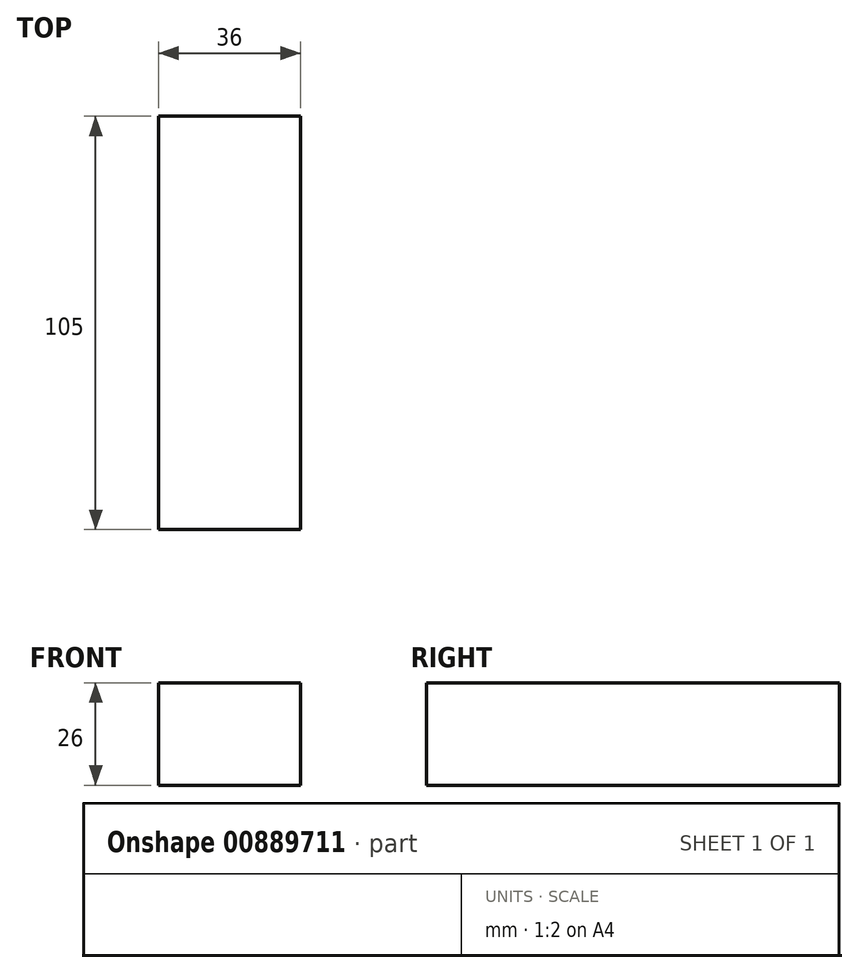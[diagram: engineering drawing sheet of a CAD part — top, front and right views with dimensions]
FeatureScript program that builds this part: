
annotation { "Feature Type Name" : "Feature", "Feature Type Description" : "" }
export const myFeature = defineFeature(function(context is Context, id is Id, definition is map)
    precondition{}
    {
        {
            var Q0;
            Q0=qCreatedBy(makeId("Top.planeOp"), FACE);
            var sketch = newSketch(context, id + "F0", { "sketchPlane" : qUnion([Q0])});
            skLineSegment(sketch, "E0.bottom", {"start": v(18, -52.5) * mm, "end": v(-18, -52.5) * mm});
            skLineSegment(sketch, "E0.top", {"start": v(18, 52.5) * mm, "end": v(-18, 52.5) * mm});
            skLineSegment(sketch, "E0.left", {"start": v(18, -52.5) * mm, "end": v(18, 52.5) * mm});
            skLineSegment(sketch, "E0.right", {"start": v(-18, -52.5) * mm, "end": v(-18, 52.5) * mm});
            skPoint(sketch, "E0.middle", {"position": v(0, 0) * mm});
            skSolve(sketch);
        }
        {
            var Q0;
            Q0 = qSketchRegion(id + "F0", true);
            extrude(context, id + "F1", {"entities" : qUnion([Q0]), "depth" : 26 * mm, "offsetDistance" : 25 * mm});
        }
    });
